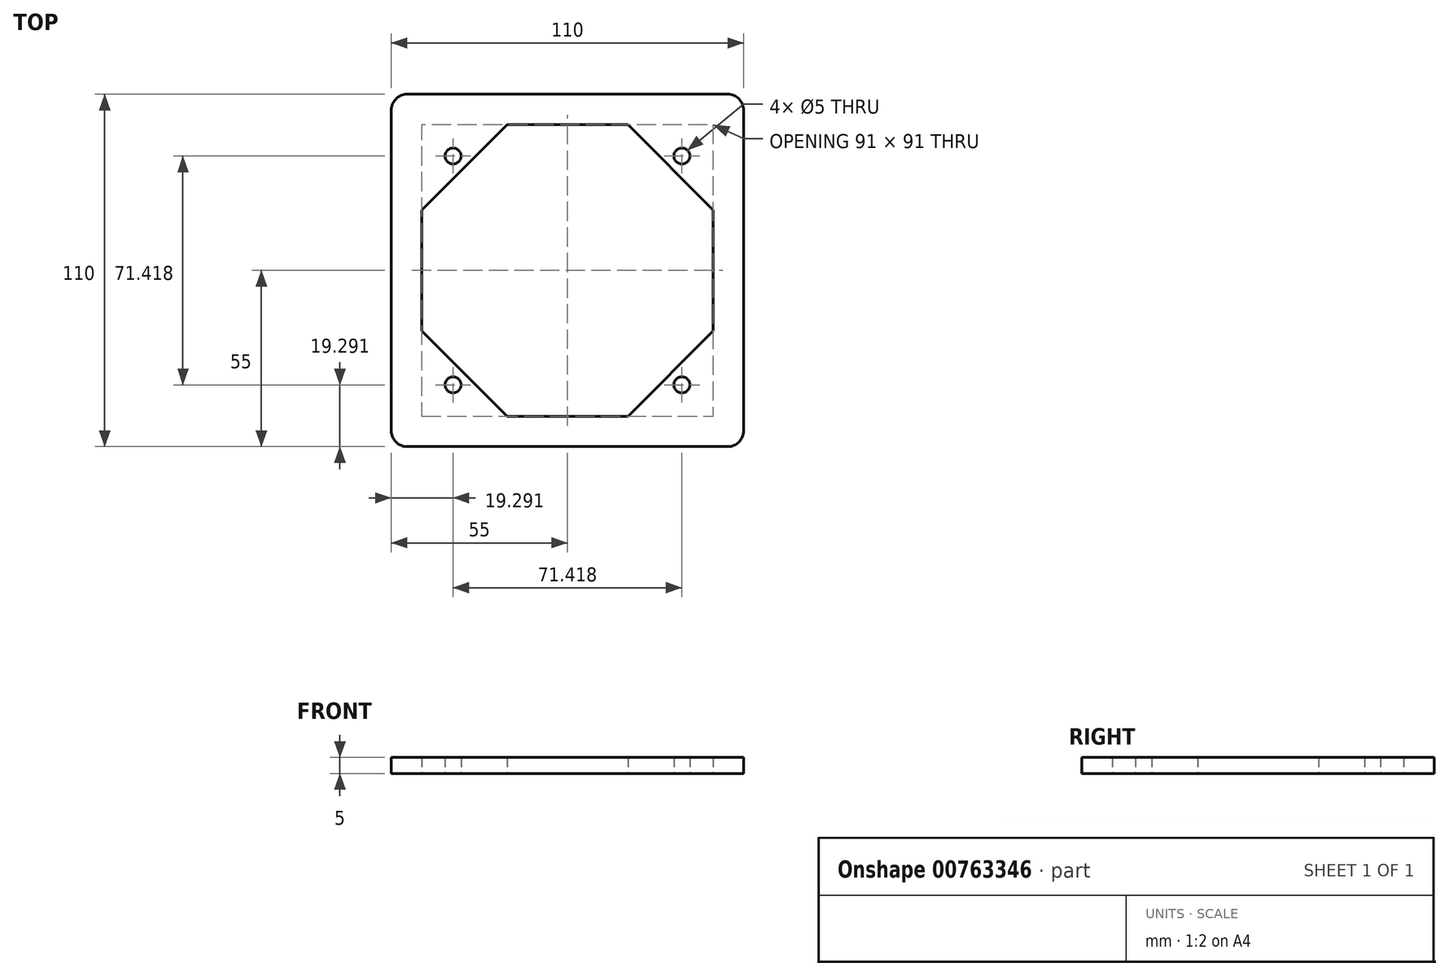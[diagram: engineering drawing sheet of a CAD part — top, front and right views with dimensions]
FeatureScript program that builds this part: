
annotation { "Feature Type Name" : "Feature", "Feature Type Description" : "" }
export const myFeature = defineFeature(function(context is Context, id is Id, definition is map)
    precondition{}
    {
        {
            var Q0;
            Q0=qCreatedBy(makeId("Top.planeOp"),FACE);
            var sketch = newSketch(context, id + "F0", { "sketchPlane" : qUnion([Q0])});
            skCircle(sketch, "E0.cCircle", {"center": v(0, 0) * mm, "radius": 45.5 * mm, "construction": true});
            skLineSegment(sketch, "E0.0", {"start": v(45.5, 18.85) * mm, "end": v(45.5, -18.85) * mm});
            skLineSegment(sketch, "E0.1", {"start": v(45.5, -18.85) * mm, "end": v(18.85, -45.5) * mm});
            skLineSegment(sketch, "E0.2", {"start": v(18.85, -45.5) * mm, "end": v(-18.85, -45.5) * mm});
            skLineSegment(sketch, "E0.3", {"start": v(-18.85, -45.5) * mm, "end": v(-45.5, -18.85) * mm});
            skLineSegment(sketch, "E0.4", {"start": v(-45.5, -18.85) * mm, "end": v(-45.5, 18.85) * mm});
            skLineSegment(sketch, "E0.5", {"start": v(-45.5, 18.85) * mm, "end": v(-18.85, 45.5) * mm});
            skLineSegment(sketch, "E0.6", {"start": v(-18.85, 45.5) * mm, "end": v(18.85, 45.5) * mm});
            skLineSegment(sketch, "E0.7", {"start": v(18.85, 45.5) * mm, "end": v(45.5, 18.85) * mm});
            skPoint(sketch, "E0.0.midPoint", {"position": v(45.5, 0) * mm});
            skLineSegment(sketch, "E1.bottom", {"start": v(50, -55) * mm, "end": v(-50, -55) * mm});
            skLineSegment(sketch, "E1.top", {"start": v(50, 55) * mm, "end": v(-50, 55) * mm});
            skLineSegment(sketch, "E1.left", {"start": v(55, -50) * mm, "end": v(55, 50) * mm});
            skLineSegment(sketch, "E1.right", {"start": v(-55, -50) * mm, "end": v(-55, 50) * mm});
            skLineSegment(sketch, "E2", {"start": v(-55, -55) * mm, "end": v(55, 55) * mm, "construction": true});
            skCircle(sketch, "E3.cCircle", {"center": v(0, 0) * mm, "radius": 50.5 * mm, "construction": true});
            skLineSegment(sketch, "E3.0", {"start": v(35.7, 35.7) * mm, "end": v(35.7, -35.7) * mm, "construction": true});
            skLineSegment(sketch, "E3.1", {"start": v(35.7, -35.7) * mm, "end": v(-35.7, -35.7) * mm, "construction": true});
            skLineSegment(sketch, "E3.2", {"start": v(-35.7, -35.7) * mm, "end": v(-35.7, 35.7) * mm, "construction": true});
            skLineSegment(sketch, "E3.3", {"start": v(-35.7, 35.7) * mm, "end": v(35.7, 35.7) * mm, "construction": true});
            skCircle(sketch, "E4", {"center": v(-35.7, 35.7) * mm, "radius": 2.5 * mm});
            skCircle(sketch, "E5", {"center": v(35.7, 35.7) * mm, "radius": 2.5 * mm});
            skCircle(sketch, "E6", {"center": v(35.7, -35.7) * mm, "radius": 2.5 * mm});
            skCircle(sketch, "E7", {"center": v(-35.7, -35.7) * mm, "radius": 2.5 * mm});
            skPoint(sketch, "E8.visualSharp", {"position": v(-55, 55) * mm});
            skArc(sketch, "E8.filletArc", {"start": v(-50, 55) * mm, "mid": v(-53.54, 53.54) * mm, "end": v(-55, 50) * mm});
            skPoint(sketch, "E9.visualSharp", {"position": v(55, 55) * mm});
            skArc(sketch, "E9.filletArc", {"start": v(55, 50) * mm, "mid": v(53.54, 53.54) * mm, "end": v(50, 55) * mm});
            skPoint(sketch, "E10.visualSharp", {"position": v(55, -55) * mm});
            skArc(sketch, "E10.filletArc", {"start": v(50, -55) * mm, "mid": v(53.54, -53.54) * mm, "end": v(55, -50) * mm});
            skPoint(sketch, "E11.visualSharp", {"position": v(-55, -55) * mm});
            skArc(sketch, "E11.filletArc", {"start": v(-55, -50) * mm, "mid": v(-53.54, -53.54) * mm, "end": v(-50, -55) * mm});
            skSolve(sketch);
        }
        {
            var Q0;
            Q0 = qSketchRegion(id + "F0", true);
            extrude(context, id + "F1", {"entities" : qUnion([Q0]), "depth" : 5 * mm, "offsetDistance" : 25 * mm});
        }
    });
